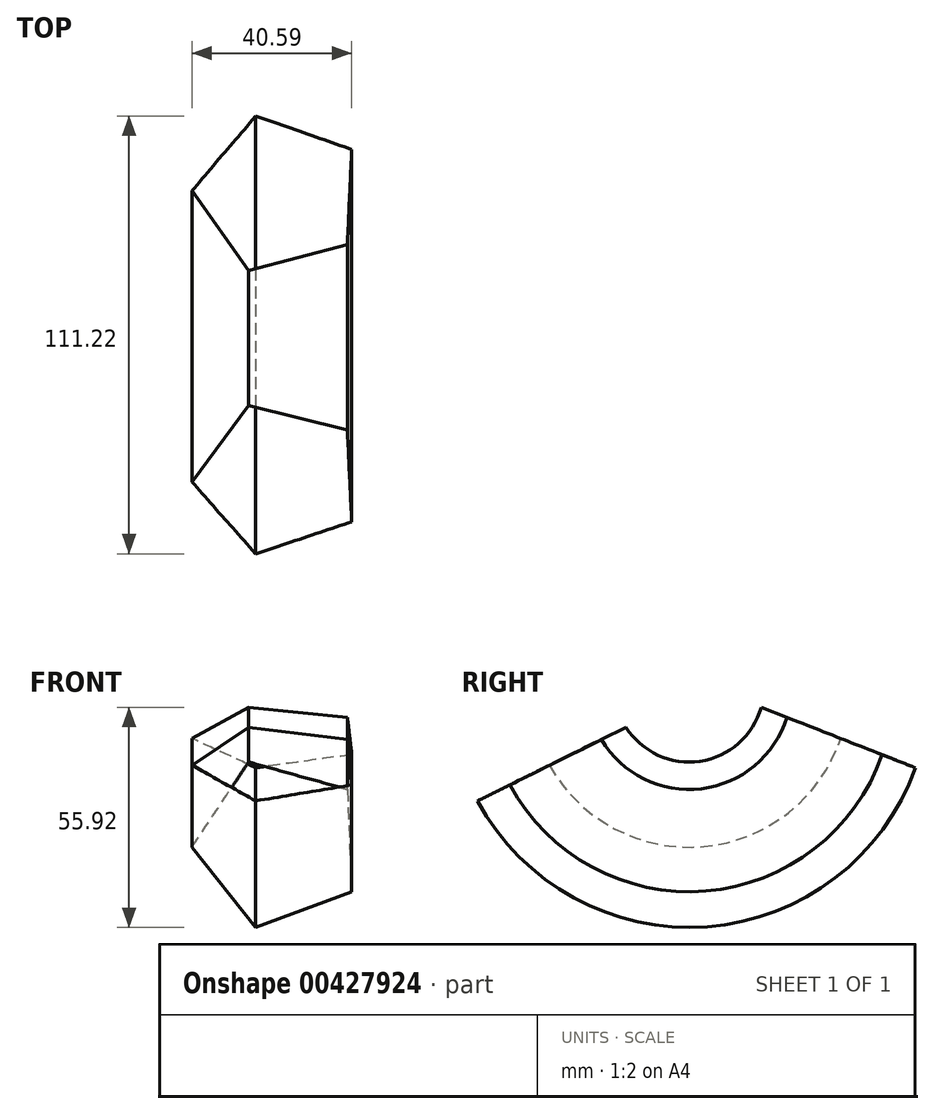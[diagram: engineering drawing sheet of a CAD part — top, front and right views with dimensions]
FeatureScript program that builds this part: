
annotation { "Feature Type Name" : "Feature", "Feature Type Description" : "" }
export const myFeature = defineFeature(function(context is Context, id is Id, definition is map)
    precondition{}
    {
        {
            var Q0;
            Q0=qCreatedBy(makeId("Front.planeOp"),FACE);
            var sketch = newSketch(context, id + "F0", { "sketchPlane" : qUnion([Q0])});
            skCircle(sketch, "E0.cCircle", {"center": v(0, 0) * mm, "radius": 17.92 * mm, "construction": true});
            skLineSegment(sketch, "E0.0", {"start": v(-22.13, -0.95) * mm, "end": v(-7.74, 20.76) * mm});
            skLineSegment(sketch, "E0.1", {"start": v(-7.74, 20.76) * mm, "end": v(17.35, 13.77) * mm});
            skLineSegment(sketch, "E0.2", {"start": v(17.35, 13.77) * mm, "end": v(18.46, -12.24) * mm});
            skLineSegment(sketch, "E0.3", {"start": v(18.46, -12.24) * mm, "end": v(-5.94, -21.34) * mm});
            skLineSegment(sketch, "E0.4", {"start": v(-5.94, -21.34) * mm, "end": v(-22.13, -0.95) * mm});
            skPoint(sketch, "E0.0.midPoint", {"position": v(-14.94, 9.9) * mm});
            skSolve(sketch);
        }
        {
            var Q0;
            Q0=qCreatedBy(makeId("Right.planeOp"),FACE);
            var sketch = newSketch(context, id + "F1", { "sketchPlane" : qUnion([Q0])});
            skArc(sketch, "E1", {"start": v(-36.58, 20.27) * mm, "mid": v(1.72, 0.12) * mm, "end": v(35.66, 26.97) * mm});
            skSolve(sketch);
        }
        {
            var Q0;
            Q0 = qSketchRegion(id + "F0", true);
            var Q1;
            Q1=sQuery(id+"F0.wireOp",EDGE,"E0.2");
            var Q2;
            Q2=sQuery(id+"F0.wireOp",EDGE,"E0.1");
            var Q3;
            Q3=sQuery(id+"F0.wireOp",EDGE,"E0.4");
            var Q4;
            Q4=sQuery(id+"F0.wireOp",EDGE,"E0.3");
            var Q5;
            Q5=sQuery(id+"F0.wireOp",EDGE,"E0.0");
            var Q6;
            Q6 = qConstructionFilter(qBodyType(qCreatedBy(id + "F1" ,EDGE), BodyType.WIRE), ConstructionObject.NO);
            sweep(context, id + "F2", {"bodyType" : ToolBodyType.SURFACE, "profiles" : qUnion([Q0]), "surfaceProfiles" : qUnion([Q1, Q2, Q3, Q4, Q5]), "path" : qUnion([Q6])});
        }
    });
